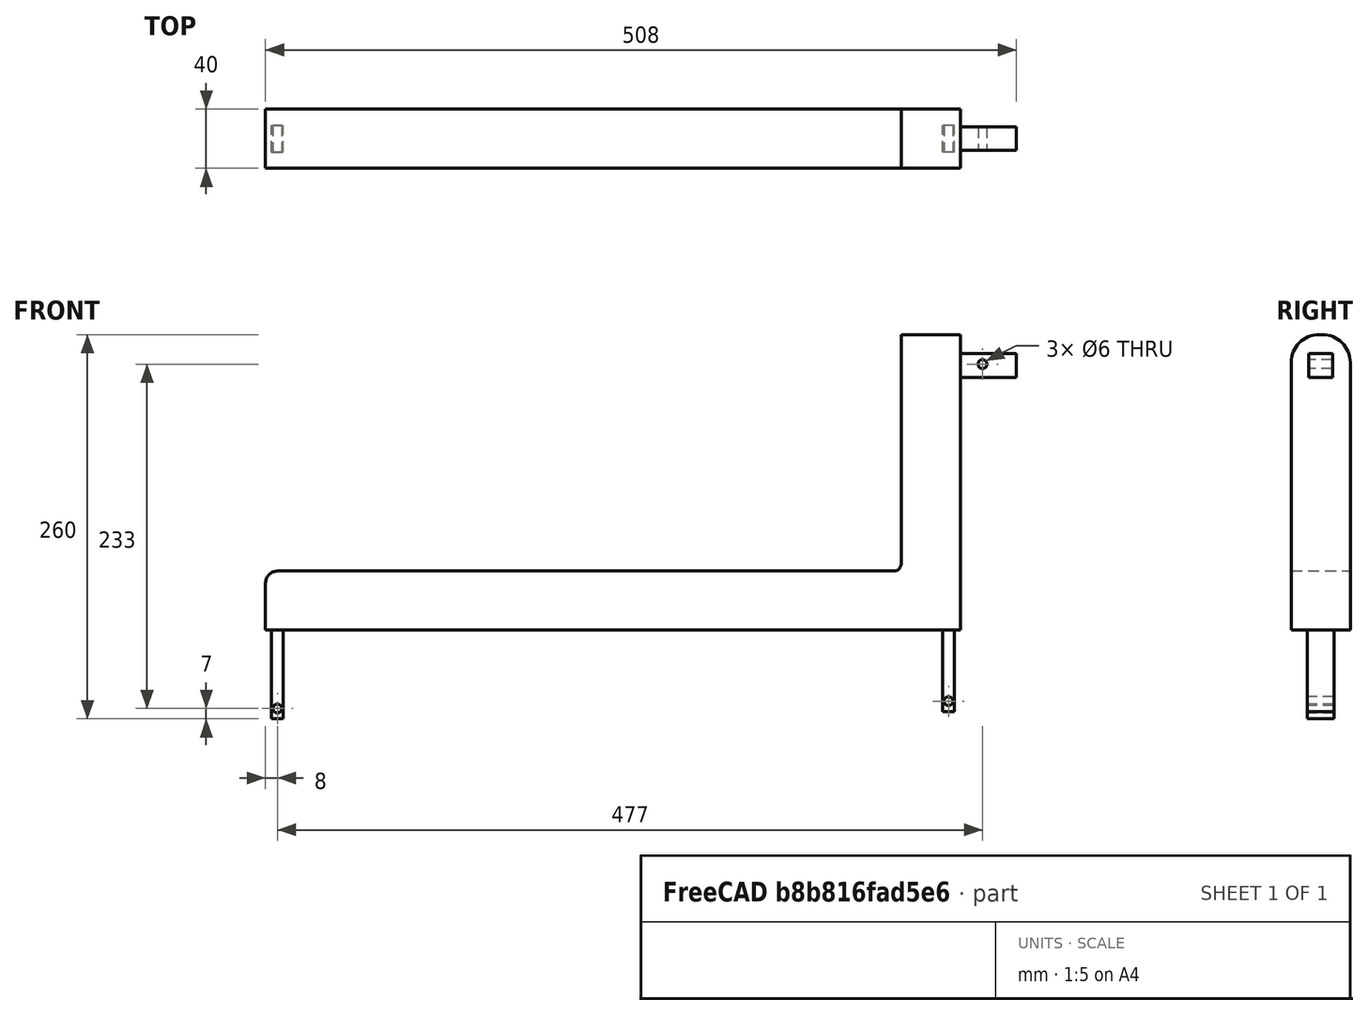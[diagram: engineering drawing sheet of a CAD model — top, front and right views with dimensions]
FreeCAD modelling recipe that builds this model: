
FCSTD DOCUMENT  (FreeCAD 0.16R6704 (Git))
Label: Object 2
License: All rights reserved
LicenseURL: http://en.wikipedia.org/wiki/All_rights_reserved
objects: Part::Box×5, Part::MultiFuse×3, Part::Cylinder×3, Part::Cut×3, Part::Fillet×3
note: 17 computed .brp shape members not serialized (recipe doc carries the construction recipe); baked Part::Feature solids carry a one-line shape summary decoded from their .brp

FEATURE [Part::Box] Box105  label="Cubo071"
  Height = 60
  Length = 8
  Placement = pos=(-22,-9,525) rot=(0,0,1;0rad)
  Width = 18
FEATURE [Part::Box] Box106  label="Cubo072"
  Height = 40
  Length = 470
  Placement = pos=(-480,-20,585) rot=(0,0,1;0rad)
  Width = 40
FEATURE [Part::Box] Box107  label="Cubo073"
  Height = 200
  Length = 40
  Placement = pos=(-50,-20,585) rot=(0,0,1;0rad)
  Width = 40
FEATURE [Part::Box] Box109  label="Cubo075"
  Height = 16
  Length = 38
  Placement = pos=(-10,-8,756) rot=(0,0,1;0rad)
  Width = 16
FEATURE [Part::MultiFuse] Fusion054
  Shapes = -> [Box107,Box109]
FEATURE [Part::Cylinder] Cylinder178  label="Cilindro102"
  Angle = 360
  Height = 60
  Placement = pos=(5,37,765) rot=(1,0,0;1.5708rad)
  Radius = 3
FEATURE [Part::Cut] Cut220  label="cut001"
  Base = -> Fusion054
  Tool = -> Cylinder178
FEATURE [Part::Cylinder] Cylinder179  label="Cilindro103"
  Angle = 360
  Height = 60
  Placement = pos=(-18,30,532) rot=(1,0,0;1.5708rad)
  Radius = 3
FEATURE [Part::Cut] Cut221  label="saliente001"
  Base = -> Box105
  Placement = pos=(0,0,5) rot=(0,0,1;0rad)
  Tool = -> Cylinder179
FEATURE [Part::Box] Box110  label="Cubo076"
  Height = 60
  Length = 8
  Placement = pos=(-22,-9,525) rot=(0,0,1;0rad)
  Width = 18
FEATURE [Part::Cylinder] Cylinder180  label="Cilindro104"
  Angle = 360
  Height = 60
  Placement = pos=(-18,30,532) rot=(1,0,0;1.5708rad)
  Radius = 3
FEATURE [Part::Cut] Cut222  label="Saliente001"
  Base = -> Box110
  Placement = pos=(-454,0,0) rot=(0,0,1;0rad)
  Tool = -> Cylinder180
FEATURE [Part::MultiFuse] Fusion055
  Shapes = -> [Box106,Cut222,Cut221]
FEATURE [Part::MultiFuse] Fusion059  label="Pieza de arriba001"
  Placement = pos=(0,460,0) rot=(0,0,1;0rad)
  Shapes = -> [Fusion055,Cut220]
FEATURE [Part::Fillet] Fillet
  Base = -> Fusion059
  Edges = 2 edges r=19: [Edge11,Edge13]
FEATURE [Part::Fillet] Fillet001
  Base = -> Fillet
  Edges = 1 edges r=5: [Edge3]
FEATURE [Part::Fillet] Fillet002
  Base = -> Fillet001
  Edges = 1 edges r=8: [Edge25]
